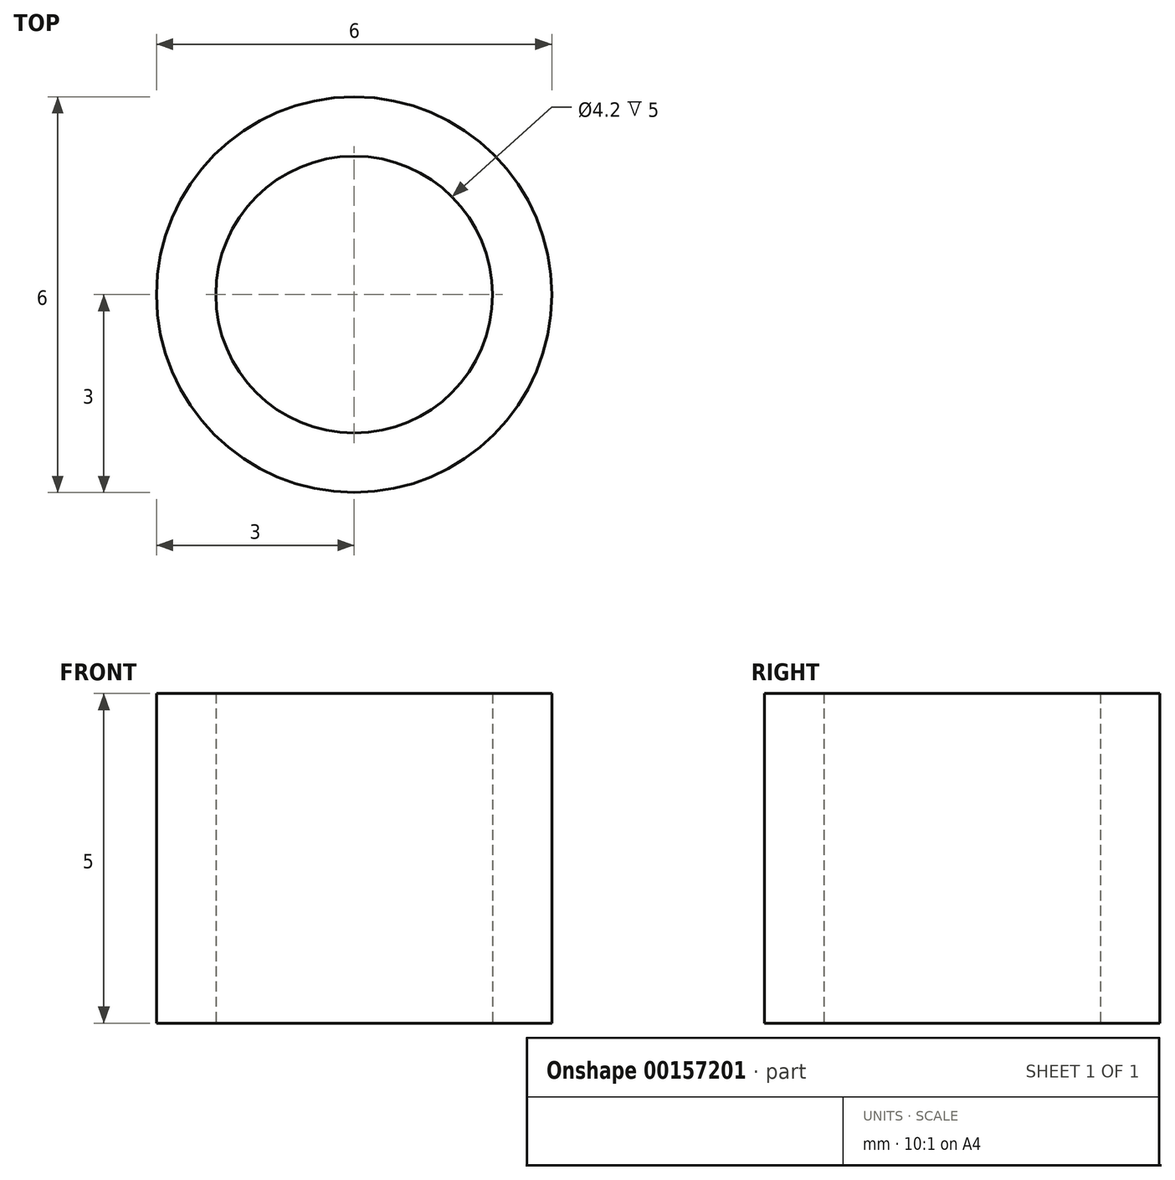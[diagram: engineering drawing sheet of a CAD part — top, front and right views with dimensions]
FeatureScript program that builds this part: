
annotation { "Feature Type Name" : "Feature", "Feature Type Description" : "" }
export const myFeature = defineFeature(function(context is Context, id is Id, definition is map)
    precondition{}
    {
        {
            var Q0;
            Q0=qCreatedBy(makeId("Top.planeOp"),FACE);
            var sketch = newSketch(context, id + "F0", { "sketchPlane" : qUnion([Q0])});
            skCircle(sketch, "E0", {"center": v(0, 0) * mm, "radius": 2.1 * mm});
            skCircle(sketch, "E1", {"center": v(0, 0) * mm, "radius": 3 * mm});
            skSolve(sketch);
        }
        {
            var Q0;
            Q0 = qSketchRegion(id + "F0", true);
            extrude(context, id + "F1", {"entities" : qUnion([Q0]), "depth" : 5 * mm});
        }
    });
